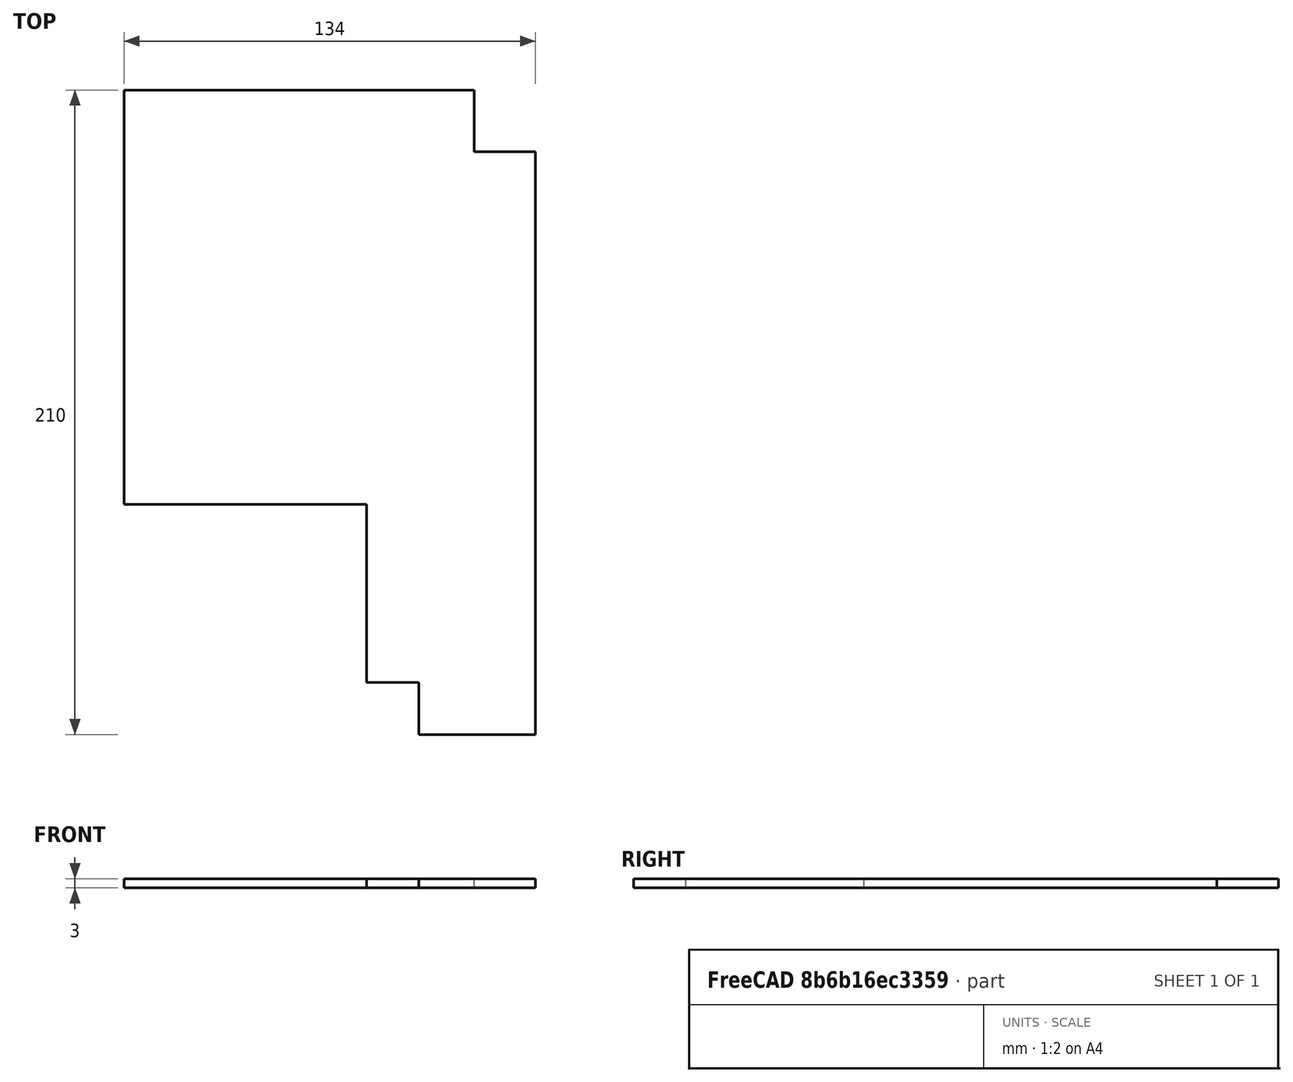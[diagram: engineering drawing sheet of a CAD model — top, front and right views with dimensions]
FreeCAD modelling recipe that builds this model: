
FCSTD DOCUMENT  (FreeCAD 0.18R)
Label: Coroplast-Right-Upper
License: CreativeCommons Attribution
LicenseURL: http://creativecommons.org/licenses/by/4.0/
objects: Sketcher::SketchObject×1, PartDesign::Pad×1, PartDesign::Body×1, App::Part×1
note: 4 computed .brp shape members not serialized (recipe doc carries the construction recipe); baked Part::Feature solids carry a one-line shape summary decoded from their .brp

FEATURE [Sketcher::SketchObject] Sketch
  MapMode = 5
  Support = -> [XY_Plane]
  sketch-geometry (10):
    g0: LineSegment StartX=155 StartY=15 StartZ=0 EndX=155 EndY=205 EndZ=0
    g1: LineSegment StartX=155 StartY=205 StartZ=0 EndX=135 EndY=205 EndZ=0
    g2: LineSegment StartX=135 StartY=225 StartZ=0 EndX=21 EndY=225 EndZ=0
    g3: LineSegment StartX=21 StartY=90 StartZ=0 EndX=100 EndY=90 EndZ=0
    g4: LineSegment StartX=135 StartY=225 StartZ=0 EndX=135 EndY=205 EndZ=0
    g5: LineSegment StartX=100 StartY=90 StartZ=0 EndX=100 EndY=32 EndZ=0
    g6: LineSegment StartX=117 StartY=15 StartZ=0 EndX=155 EndY=15 EndZ=0
    g7: LineSegment StartX=100 StartY=32 StartZ=0 EndX=117 EndY=32 EndZ=0
    g8: LineSegment StartX=117 StartY=32 StartZ=0 EndX=117 EndY=15 EndZ=0
    g9: LineSegment StartX=21 StartY=225 StartZ=0 EndX=21 EndY=90 EndZ=0
  constraints (30):
    c: Coincident(g0,g1)
    c: Vertical(g0)
    c: Horizontal(g2)
    c: Horizontal(g3)
    c: Horizontal(g1)
    c: Coincident(g2,g4)
    c: Coincident(g4,g1)
    c: Vertical(g4)
    c: DistanceX(g1,g1) = 20
    c: DistanceY(g4,g4) = 20
    c: DistanceX(g-1,g0) = 155
    c: DistanceY(g-1,g2) = 225
    c: Horizontal(g6)
    c: Vertical(g5)
    c: Coincident(g0,g6)
    c: Coincident(g3,g5)
    c: DistanceY(g0,g2) = 210
    c: Coincident(g7,g8)
    c: Horizontal(g7)
    c: Vertical(g8)
    c: Coincident(g6,g8)
    c: Coincident(g5,g7)
    c: DistanceY(g8,g8) = 17
    c: DistanceX(g6,g6) = 38
    c: DistanceX(g7,g7) = 17
    c: DistanceY(g3,g2) = 135
    c: Vertical(g9)
    c: Coincident(g3,g9)
    c: Coincident(g9,g2)
    c: DistanceX(g2,g0) = 134
FEATURE [PartDesign::Pad] Pad
  Length = 3
  Length2 = 100
  Profile = -> Sketch
  Type = 0
FEATURE [PartDesign::Body] Body  label="UpperRightCoroplast"
  Group = -> [Sketch,Pad]
  Origin = -> Origin
  Tip = -> Pad
FEATURE [App::Part] Part
  Group = -> [Body]
  Origin = -> Origin001
